# Revit family: Wall_Sensor-PIR-HCS-Switch
name_source: partatom
category: Lighting Devices
units: mm (PartAtom-declared; Revit-internal decimal feet)

## family parameters
Cut with Voids When Loaded = No
Host = Face
Maintain Annotation Orientation = No
OmniClass Number = 23.85.80.11.27
OmniClass Title = Lighting Controls
Part Type = Normal
Room Calculation Point = No
Round Connector Dimension = Use Diameter
Shared = No

## types (6) — shared parameters
Ambient Humidity Range = 0% to 95% Relative Humidity (non-condensing)
Assembly Code = D5020120
Certifications = Listed UL and cUL
Connector Description 1 = Power Supply
Connector Description 2 = Controls
Coverage = 1,000 square-foot, 180° coverage area
Default Elevation = 48 "
Description = LightHAWK®2 Passive Infrared Wall Switch Sensor
Electrical Ratings = 120VAC; 277VAC; 347VAC
Frequency = 60 Hz
Load Classification = Lighting
Manufacturer = NX Lighting Controls
Mounting = Single-gang NEMA-style switch box, Decorator-style wall plate sold separately
Number of Poles = 1
Operating Temperature = 32° – 104°F (0° – 40°C)
Passive Infrared = Dual-element pyrometer and 12-element cylindrical RhinoTuff lens
Photocell = Natural light override range: 10-500 foot-candles
Power Factor = 1
Product Material = Plastic -  Light Almond
Time Delay = 4-30 minutes, self-adapts based on occupancy; Fixed mode: 4, 8, 15, and 30 minutes;Test mode: 5 seconds
Type Comments = Lighting Device
URL = https://www.currentlighting.com
Voltage = 120 V
Warranty = Five-year limited
Wattage = 800 VA
Weight = 0.08 kg
zz Length 1 = 1.72 "
zz Length 2 = 4.13 "
zz Length 3 = 1.7 "
zz Length 4 = 2.57 "

## per-type parameters (varying)
| type | Operating Mode | zz YesNo 1 | zz YesNo 2 |
| LHIRS0 | Single Relay, No Buttons | No | No |
| LHIRS1 | Single Relay, One Button | No | Yes |
| LHIRD0 | Dual Relay(One Input / Two Outputs), No Buttons | No | No |
| LHIRD2 | Dual Relay(One Input / Two Outputs), Two Buttons | Yes | Yes |
| LHDCIRD0 | Dual Circuit(Two Inputs / Two Outputs), No Buttons | No | No |
| LHDCIRD2 | Dual Circuit(Two Inputs / Two Outputs), Two Buttons | Yes | Yes |

note: column(s) folded — value = type name in every type: Model

## geometry (parser evidence)
native form markers: Blend x7, Sweep x5
no freeform markers — native parametric forms only
